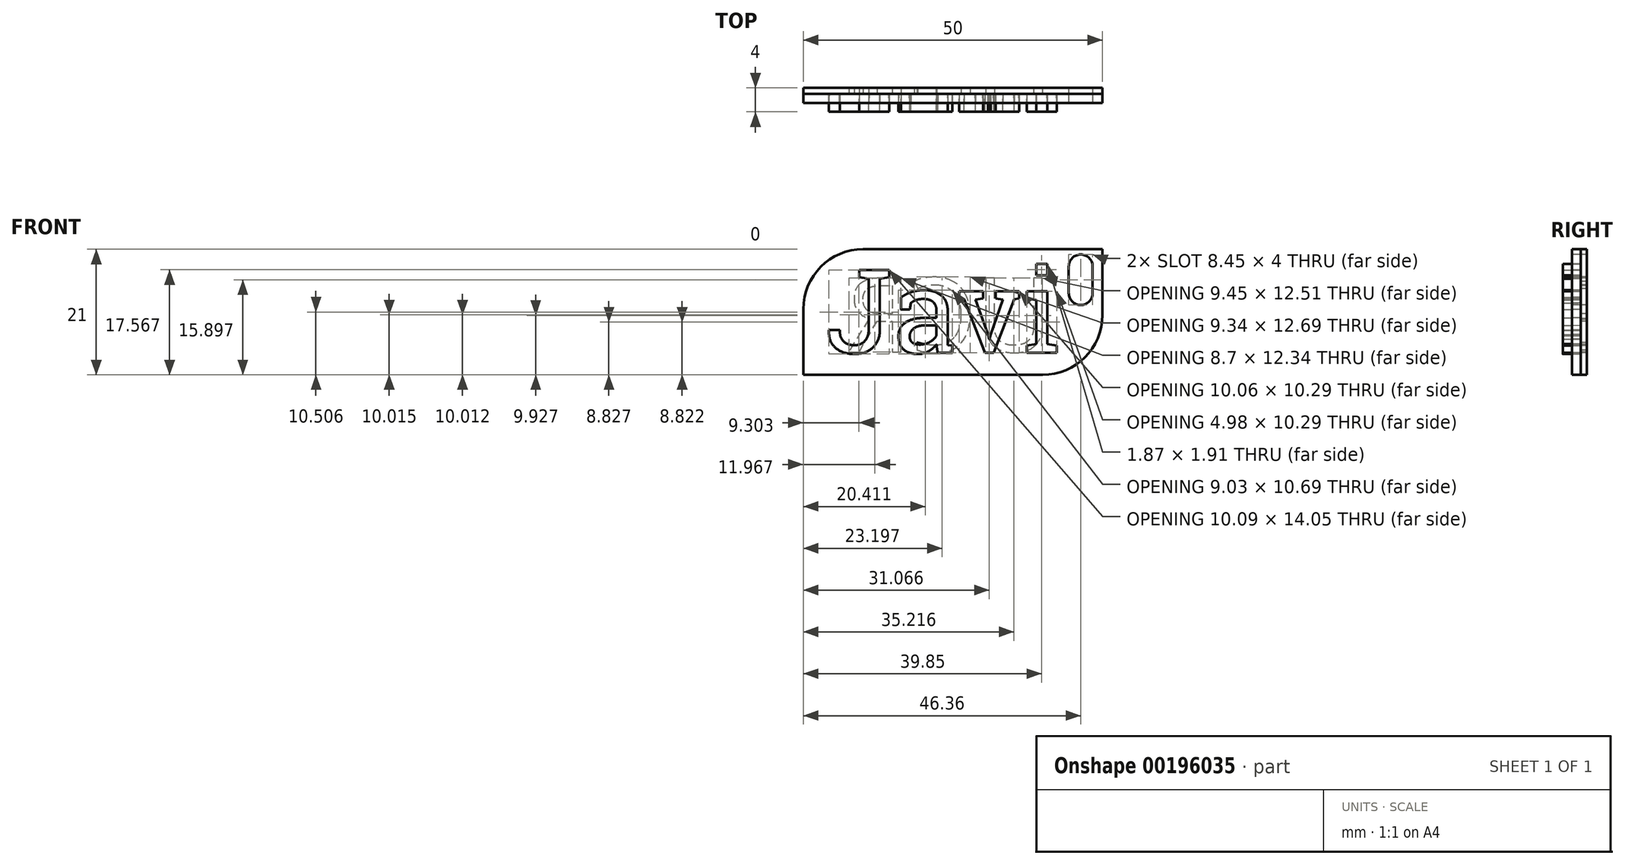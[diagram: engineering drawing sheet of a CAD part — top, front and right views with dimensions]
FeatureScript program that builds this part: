
annotation { "Feature Type Name" : "Feature", "Feature Type Description" : "" }
export const myFeature = defineFeature(function(context is Context, id is Id, definition is map)
    precondition{}
    {
        {
            var Q0;
            Q0=qCreatedBy(makeId("Front.planeOp"),FACE);
            var sketch = newSketch(context, id + "F0", { "sketchPlane" : qUnion([Q0])});
            skLineSegment(sketch, "E0.bottom", {"start": v(-27.81, 14.08) * mm, "end": v(12.19, 14.08) * mm});
            skLineSegment(sketch, "E0.top", {"start": v(-37.81, -6.92) * mm, "end": v(2.19, -6.92) * mm});
            skLineSegment(sketch, "E0.left", {"start": v(-37.81, 4.08) * mm, "end": v(-37.81, -6.92) * mm});
            skLineSegment(sketch, "E0.right", {"start": v(12.19, 14.08) * mm, "end": v(12.19, 3.08) * mm});
            skText(sketch, "E1", { "text": "Javi", "fontName": "RobotoSlab-Regular.ttf"});
            skCircle(sketch, "E2", {"center": v(8.55, 11.2) * mm, "radius": 2 * mm});
            skCircle(sketch, "E3", {"center": v(8.55, 6.75) * mm, "radius": 2 * mm});
            skLineSegment(sketch, "E4", {"start": v(8.55, 11.2) * mm, "end": v(8.55, 6.75) * mm, "construction": true});
            skLineSegment(sketch, "E5", {"start": v(6.55, 11.2) * mm, "end": v(6.55, 6.75) * mm});
            skLineSegment(sketch, "E6", {"start": v(10.55, 11.2) * mm, "end": v(10.55, 6.75) * mm});
            skPoint(sketch, "E7.visualSharp", {"position": v(-37.81, 14.08) * mm});
            skArc(sketch, "E7.filletArc", {"start": v(-27.81, 14.08) * mm, "mid": v(-34.88, 11.16) * mm, "end": v(-37.81, 4.08) * mm});
            skPoint(sketch, "E8.visualSharp", {"position": v(12.19, -6.92) * mm});
            skArc(sketch, "E8.filletArc", {"start": v(2.19, -6.92) * mm, "mid": v(9.26, -3.99) * mm, "end": v(12.19, 3.08) * mm});
            const initialGuessF0  = {"E1": [-0.03416, -0.00324, 1, 0, 0.01403]};
            skSetInitialGuess(sketch, initialGuessF0);
            skSolve(sketch);
        }
        {
            var Q0;
            Q0=makeQuery(id+"F0.imprint","IMPRINT",FACE,{"disambiguationData":[TD([[makeQuery(id+"F0.imprint","IMPRINT",EDGE,{"derivedFrom":sQuery(id+"F0.wireOp",EDGE,"E1.sketch_text.stroke-0")}),-1.0]])]});
            var Q1;
            Q1=makeQuery(id+"F0.imprint","IMPRINT",FACE,{"disambiguationData":[TD([[makeQuery(id+"F0.imprint","IMPRINT",EDGE,{"derivedFrom":sQuery(id+"F0.wireOp",EDGE,"E1.sketch_text.stroke-18")}),-1.0]])]});
            var Q2;
            Q2=makeQuery(id+"F0.imprint","IMPRINT",FACE,{"disambiguationData":[TD([[makeQuery(id+"F0.imprint","IMPRINT",EDGE,{"derivedFrom":sQuery(id+"F0.wireOp",EDGE,"E1.sketch_text.stroke-53")}),-1.0]])]});
            var Q3;
            Q3=makeQuery(id+"F0.imprint","IMPRINT",FACE,{"disambiguationData":[TD([[makeQuery(id+"F0.imprint","IMPRINT",EDGE,{"derivedFrom":sQuery(id+"F0.wireOp",EDGE,"E1.sketch_text.stroke-71")}),-1.0]])]});
            var Q4;
            Q4=makeQuery(id+"F0.imprint","IMPRINT",FACE,{"disambiguationData":[TD([[makeQuery(id+"F0.imprint","IMPRINT",EDGE,{"derivedFrom":sQuery(id+"F0.wireOp",EDGE,"E1.sketch_text.stroke-81")}),-1.0]])]});
            extrude(context, id + "F1", {"entities" : qUnion([Q0, Q1, Q2, Q3, Q4]), "depth" : 1.5 * mm, "hasSecondDirection" : true, "secondDirectionOppositeDirection" : true, "secondDirectionDepth" : 1.5 * mm, "hasSecondDirectionDraft" : true, "secondDirectionDraftAngle" : 2 * degree, "secondDirectionDraftPullDirection" : true});
        }
        {
            var Q0;
            Q0 = qSketchRegion(id + "F0", true);
            extrude(context, id + "F2", {"entities" : qUnion([Q0]), "oppositeDirection" : true, "depth" : 1.5 * mm});
        }
        {
            var Q0;
            Q0=makeQuery(id+"F2.opExtrude","CAP_FACE",FACE,{"disambiguationData":[OSD([sQuery(id+"F0.wireOp",EDGE,"E0.bottom"),sQuery(id+"F0.wireOp",EDGE,"E0.top"),sQuery(id+"F0.wireOp",EDGE,"E0.left"),sQuery(id+"F0.wireOp",EDGE,"E0.right"),sQuery(id+"F0.wireOp",EDGE,"E1.sketch_text.stroke-0"),sQuery(id+"F0.wireOp",EDGE,"E1.sketch_text.stroke-1"),sQuery(id+"F0.wireOp",EDGE,"E1.sketch_text.stroke-2"),sQuery(id+"F0.wireOp",EDGE,"E1.sketch_text.stroke-3"),sQuery(id+"F0.wireOp",EDGE,"E1.sketch_text.stroke-4"),sQuery(id+"F0.wireOp",EDGE,"E1.sketch_text.stroke-5"),sQuery(id+"F0.wireOp",EDGE,"E1.sketch_text.stroke-6"),sQuery(id+"F0.wireOp",EDGE,"E1.sketch_text.stroke-7"),sQuery(id+"F0.wireOp",EDGE,"E1.sketch_text.stroke-8"),sQuery(id+"F0.wireOp",EDGE,"E1.sketch_text.stroke-9"),sQuery(id+"F0.wireOp",EDGE,"E1.sketch_text.stroke-10"),sQuery(id+"F0.wireOp",EDGE,"E1.sketch_text.stroke-11"),sQuery(id+"F0.wireOp",EDGE,"E1.sketch_text.stroke-12"),sQuery(id+"F0.wireOp",EDGE,"E1.sketch_text.stroke-13"),sQuery(id+"F0.wireOp",EDGE,"E1.sketch_text.stroke-14"),sQuery(id+"F0.wireOp",EDGE,"E1.sketch_text.stroke-15"),sQuery(id+"F0.wireOp",EDGE,"E1.sketch_text.stroke-16"),sQuery(id+"F0.wireOp",EDGE,"E1.sketch_text.stroke-17"),sQuery(id+"F0.wireOp",EDGE,"E1.sketch_text.stroke-18"),sQuery(id+"F0.wireOp",EDGE,"E1.sketch_text.stroke-19"),sQuery(id+"F0.wireOp",EDGE,"E1.sketch_text.stroke-20"),sQuery(id+"F0.wireOp",EDGE,"E1.sketch_text.stroke-21"),sQuery(id+"F0.wireOp",EDGE,"E1.sketch_text.stroke-22"),sQuery(id+"F0.wireOp",EDGE,"E1.sketch_text.stroke-23"),sQuery(id+"F0.wireOp",EDGE,"E1.sketch_text.stroke-24"),sQuery(id+"F0.wireOp",EDGE,"E1.sketch_text.stroke-25"),sQuery(id+"F0.wireOp",EDGE,"E1.sketch_text.stroke-26"),sQuery(id+"F0.wireOp",EDGE,"E1.sketch_text.stroke-27"),sQuery(id+"F0.wireOp",EDGE,"E1.sketch_text.stroke-28"),sQuery(id+"F0.wireOp",EDGE,"E1.sketch_text.stroke-29"),sQuery(id+"F0.wireOp",EDGE,"E1.sketch_text.stroke-30"),sQuery(id+"F0.wireOp",EDGE,"E1.sketch_text.stroke-31"),sQuery(id+"F0.wireOp",EDGE,"E1.sketch_text.stroke-32"),sQuery(id+"F0.wireOp",EDGE,"E1.sketch_text.stroke-33"),sQuery(id+"F0.wireOp",EDGE,"E1.sketch_text.stroke-34"),sQuery(id+"F0.wireOp",EDGE,"E1.sketch_text.stroke-35"),sQuery(id+"F0.wireOp",EDGE,"E1.sketch_text.stroke-36"),sQuery(id+"F0.wireOp",EDGE,"E1.sketch_text.stroke-37"),sQuery(id+"F0.wireOp",EDGE,"E1.sketch_text.stroke-38"),sQuery(id+"F0.wireOp",EDGE,"E1.sketch_text.stroke-39"),sQuery(id+"F0.wireOp",EDGE,"E1.sketch_text.stroke-40"),sQuery(id+"F0.wireOp",EDGE,"E1.sketch_text.stroke-41"),sQuery(id+"F0.wireOp",EDGE,"E1.sketch_text.stroke-42"),sQuery(id+"F0.wireOp",EDGE,"E1.sketch_text.stroke-43"),sQuery(id+"F0.wireOp",EDGE,"E1.sketch_text.stroke-44"),sQuery(id+"F0.wireOp",EDGE,"E1.sketch_text.stroke-53"),sQuery(id+"F0.wireOp",EDGE,"E1.sketch_text.stroke-54"),sQuery(id+"F0.wireOp",EDGE,"E1.sketch_text.stroke-55"),sQuery(id+"F0.wireOp",EDGE,"E1.sketch_text.stroke-56"),sQuery(id+"F0.wireOp",EDGE,"E1.sketch_text.stroke-57"),sQuery(id+"F0.wireOp",EDGE,"E1.sketch_text.stroke-58"),sQuery(id+"F0.wireOp",EDGE,"E1.sketch_text.stroke-59"),sQuery(id+"F0.wireOp",EDGE,"E1.sketch_text.stroke-60"),sQuery(id+"F0.wireOp",EDGE,"E1.sketch_text.stroke-61"),sQuery(id+"F0.wireOp",EDGE,"E1.sketch_text.stroke-62"),sQuery(id+"F0.wireOp",EDGE,"E1.sketch_text.stroke-63"),sQuery(id+"F0.wireOp",EDGE,"E1.sketch_text.stroke-64"),sQuery(id+"F0.wireOp",EDGE,"E1.sketch_text.stroke-65"),sQuery(id+"F0.wireOp",EDGE,"E1.sketch_text.stroke-66"),sQuery(id+"F0.wireOp",EDGE,"E1.sketch_text.stroke-67"),sQuery(id+"F0.wireOp",EDGE,"E1.sketch_text.stroke-68"),sQuery(id+"F0.wireOp",EDGE,"E1.sketch_text.stroke-69"),sQuery(id+"F0.wireOp",EDGE,"E1.sketch_text.stroke-70"),sQuery(id+"F0.wireOp",EDGE,"E1.sketch_text.stroke-71"),sQuery(id+"F0.wireOp",EDGE,"E1.sketch_text.stroke-72"),sQuery(id+"F0.wireOp",EDGE,"E1.sketch_text.stroke-73"),sQuery(id+"F0.wireOp",EDGE,"E1.sketch_text.stroke-74"),sQuery(id+"F0.wireOp",EDGE,"E1.sketch_text.stroke-75"),sQuery(id+"F0.wireOp",EDGE,"E1.sketch_text.stroke-76"),sQuery(id+"F0.wireOp",EDGE,"E1.sketch_text.stroke-77"),sQuery(id+"F0.wireOp",EDGE,"E1.sketch_text.stroke-78"),sQuery(id+"F0.wireOp",EDGE,"E1.sketch_text.stroke-79"),sQuery(id+"F0.wireOp",EDGE,"E1.sketch_text.stroke-80"),sQuery(id+"F0.wireOp",EDGE,"E1.sketch_text.stroke-81"),sQuery(id+"F0.wireOp",EDGE,"E1.sketch_text.stroke-82"),sQuery(id+"F0.wireOp",EDGE,"E1.sketch_text.stroke-83"),sQuery(id+"F0.wireOp",EDGE,"E1.sketch_text.stroke-84"),sQuery(id+"F0.wireOp",EDGE,"E2"),sQuery(id+"F0.wireOp",EDGE,"E3"),sQuery(id+"F0.wireOp",EDGE,"E5"),sQuery(id+"F0.wireOp",EDGE,"E6"),sQuery(id+"F0.wireOp",EDGE,"E7.filletArc"),sQuery(id+"F0.wireOp",EDGE,"E8.filletArc")])],"isStart":false});
            var sketch = newSketch(context, id + "F3", { "sketchPlane" : qUnion([Q0])});
            skText(sketch, "E9", { "text": "UCR", "fontName": "OpenSans-Regular.ttf"});
            skArc(sketch, "E10.0", {"start": v(27.81, 14.08) * mm, "mid": v(34.88, 11.16) * mm, "end": v(37.81, 4.08) * mm});
            skLineSegment(sketch, "E10.1", {"start": v(37.81, 4.08) * mm, "end": v(37.81, -6.92) * mm});
            skLineSegment(sketch, "E10.2", {"start": v(37.81, -6.92) * mm, "end": v(-2.19, -6.92) * mm});
            skArc(sketch, "E10.3", {"start": v(-2.19, -6.92) * mm, "mid": v(-9.26, -3.99) * mm, "end": v(-12.19, 3.08) * mm});
            skLineSegment(sketch, "E10.4", {"start": v(-12.19, 14.08) * mm, "end": v(-12.19, 3.08) * mm});
            skLineSegment(sketch, "E10.5", {"start": v(27.81, 14.08) * mm, "end": v(-12.19, 14.08) * mm});
            skLineSegment(sketch, "E10.6", {"start": v(-6.55, 11.2) * mm, "end": v(-6.55, 6.75) * mm});
            skArc(sketch, "E10.7", {"start": v(-10.55, 11.2) * mm, "mid": v(-8.55, 13.2) * mm, "end": v(-6.55, 11.2) * mm});
            skArc(sketch, "E10.8", {"start": v(-6.55, 6.75) * mm, "mid": v(-8.55, 4.75) * mm, "end": v(-10.55, 6.75) * mm});
            skLineSegment(sketch, "E10.9", {"start": v(-10.55, 11.2) * mm, "end": v(-10.55, 6.75) * mm});
            const initialGuessF3  = {"E9": [-0.0037, -0.00308, 1, 0, 0.01245]};
            skSetInitialGuess(sketch, initialGuessF3);
            skSolve(sketch);
        }
        {
            var Q0;
            {var subQ23=sQuery(id+"F3.wireOp",EDGE,"E9.sketch_text.stroke-0");Q0=makeQuery(id+"F3.imprint","IMPRINT",FACE,{"disambiguationData":[TD([[makeQuery(id+"F3.imprint","IMPRINT",EDGE,{"derivedFrom":subQ23}),1.0]])]});}
            var Q1;
            {var subQ1=sQuery(id+"F3.wireOp",EDGE,"E9.sketch_text.stroke-37");Q1=makeQuery(id+"F3.imprint","IMPRINT",FACE,{"disambiguationData":[TD([[makeQuery(id+"F3.imprint","IMPRINT",EDGE,{"derivedFrom":subQ1}),1.0]])]});}
            var Q2;
            {var subQ0=makeQuery(id+"F2.opExtrude","CAP_EDGE",EDGE,{"disambiguationData":[OSD([sQuery(id+"F0.wireOp",EDGE,"E1.sketch_text.stroke-0")])],"isStart":false});Q2=makeQuery(id+"F3.imprint","IMPRINT",FACE,{"disambiguationData":[TD([[makeQuery(id+"F3.imprint","IMPRINT",EDGE,{"derivedFrom":subQ0}),1.0]])]});}
            var Q3;
            {var subQ11=sQuery(id+"F3.wireOp",EDGE,"E9.sketch_text.stroke-18");Q3=makeQuery(id+"F3.imprint","IMPRINT",FACE,{"disambiguationData":[TD([[makeQuery(id+"F3.imprint","IMPRINT",EDGE,{"derivedFrom":subQ11}),1.0]])]});}
            var Q4;
            {var subQ4=makeQuery(id+"F2.opExtrude","CAP_EDGE",EDGE,{"disambiguationData":[OSD([sQuery(id+"F0.wireOp",EDGE,"E1.sketch_text.stroke-59")])],"isStart":false});Q4=makeQuery(id+"F3.imprint","IMPRINT",FACE,{"disambiguationData":[TD([[makeQuery(id+"F3.imprint","IMPRINT",EDGE,{"derivedFrom":subQ4}),1.0]])]});}
            var Q5;
            {var subQ0=makeQuery(id+"F2.opExtrude","CAP_EDGE",EDGE,{"disambiguationData":[OSD([sQuery(id+"F0.wireOp",EDGE,"E1.sketch_text.stroke-53")])],"isStart":false});Q5=makeQuery(id+"F3.imprint","IMPRINT",FACE,{"disambiguationData":[TD([[makeQuery(id+"F3.imprint","IMPRINT",EDGE,{"derivedFrom":subQ0}),1.0]])]});}
            var Q6;
            {var subQ1=sQuery(id+"F3.wireOp",EDGE,"E9.sketch_text.stroke-4");Q6=makeQuery(id+"F3.imprint","IMPRINT",FACE,{"disambiguationData":[TD([[makeQuery(id+"F3.imprint","IMPRINT",EDGE,{"derivedFrom":subQ1}),1.0]])]});}
            var Q7;
            Q7=makeQuery(id+"F3.imprint","IMPRINT",FACE,{"disambiguationData":[TD([[makeQuery(id+"F3.imprint","IMPRINT",EDGE,{"derivedFrom":makeQuery(id+"F2.opExtrude","CAP_EDGE",EDGE,{"disambiguationData":[OSD([sQuery(id+"F0.wireOp",EDGE,"E1.sketch_text.stroke-81")])],"isStart":false})}),1.0]])]});
            var Q8;
            {var subQ5=makeQuery(id+"F2.opExtrude","CAP_EDGE",EDGE,{"disambiguationData":[OSD([sQuery(id+"F0.wireOp",EDGE,"E1.sketch_text.stroke-74")])],"isStart":false});Q8=makeQuery(id+"F3.imprint","IMPRINT",FACE,{"disambiguationData":[TD([[makeQuery(id+"F3.imprint","IMPRINT",EDGE,{"derivedFrom":subQ5}),1.0]])]});}
            var Q9;
            {var subQ1=sQuery(id+"F3.wireOp",EDGE,"E9.sketch_text.stroke-42");Q9=makeQuery(id+"F3.imprint","IMPRINT",FACE,{"disambiguationData":[TD([[makeQuery(id+"F3.imprint","IMPRINT",EDGE,{"derivedFrom":subQ1}),1.0]])]});}
            var Q10;
            {var subQ1=sQuery(id+"F3.wireOp",EDGE,"E9.sketch_text.stroke-40");Q10=makeQuery(id+"F3.imprint","IMPRINT",FACE,{"disambiguationData":[TD([[makeQuery(id+"F3.imprint","IMPRINT",EDGE,{"derivedFrom":subQ1}),1.0]])]});}
            var Q11;
            {var subQ0=sQuery(id+"F3.wireOp",EDGE,"E9.sketch_text.stroke-41");var subQ1=makeQuery(id+"F2.opExtrude","CAP_EDGE",EDGE,{"disambiguationData":[OSD([sQuery(id+"F0.wireOp",EDGE,"E1.sketch_text.stroke-2")])],"isStart":false});var subQ2=makeQuery(id+"F3.imprint","INTERSECT",VERTEX,{"derivedFrom":[subQ1,subQ0]});Q11=makeQuery(id+"F3.imprint","IMPRINT",FACE,{"disambiguationData":[TD([[makeQuery(id+"F3.imprint","IMPRINT",EDGE,{"disambiguationData":[TD([[subQ2,-1.0]])],"derivedFrom":subQ0}),1.0]])]});}
            var Q12;
            {var subQ0=sQuery(id+"F3.wireOp",EDGE,"E9.sketch_text.stroke-21");var subQ1=makeQuery(id+"F2.opExtrude","CAP_EDGE",EDGE,{"disambiguationData":[OSD([sQuery(id+"F0.wireOp",EDGE,"E1.sketch_text.stroke-44")])],"isStart":false});var subQ2=makeQuery(id+"F3.imprint","INTERSECT",VERTEX,{"derivedFrom":[subQ1,subQ0]});Q12=makeQuery(id+"F3.imprint","IMPRINT",FACE,{"disambiguationData":[TD([[makeQuery(id+"F3.imprint","IMPRINT",EDGE,{"disambiguationData":[TD([[subQ2,-1.0]])],"derivedFrom":subQ0}),1.0]])]});}
            extrude(context, id + "F4", {"entities" : qUnion([Q0, Q1, Q2, Q3, Q4, Q5, Q6, Q7, Q8, Q9, Q10, Q11, Q12]), "depth" : 1 * mm});
        }
    });
